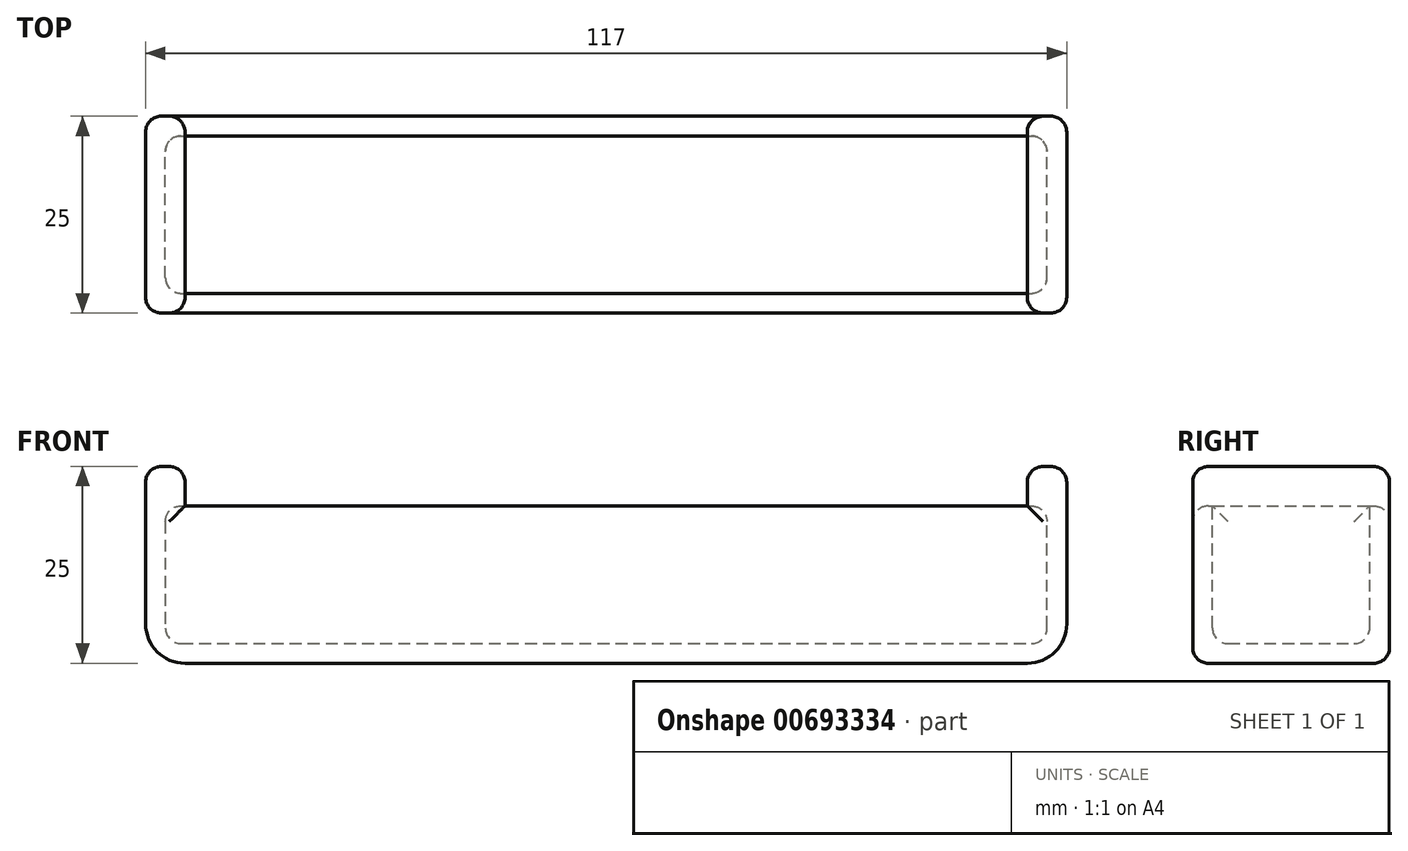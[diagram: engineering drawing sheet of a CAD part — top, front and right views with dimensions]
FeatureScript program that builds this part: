
annotation { "Feature Type Name" : "Feature", "Feature Type Description" : "" }
export const myFeature = defineFeature(function(context is Context, id is Id, definition is map)
    precondition{}
    {
        {
            var Q0;
            Q0=qCreatedBy(makeId("Front.planeOp"),FACE);
            var sketch = newSketch(context, id + "F0", { "sketchPlane" : qUnion([Q0])});
            skLineSegment(sketch, "E0", {"start": v(-39.57, 0) * mm, "end": v(67.43, 0) * mm});
            skLineSegment(sketch, "E1", {"start": v(-39.57, 0) * mm, "end": v(-39.57, 5) * mm});
            skLineSegment(sketch, "E2", {"start": v(-39.57, 5) * mm, "end": v(-44.57, 5) * mm});
            skLineSegment(sketch, "E3", {"start": v(-44.57, 5) * mm, "end": v(-44.57, -20) * mm});
            skLineSegment(sketch, "E4", {"start": v(-44.57, -20) * mm, "end": v(72.43, -20) * mm});
            skLineSegment(sketch, "E5", {"start": v(72.43, -20) * mm, "end": v(72.43, 5) * mm});
            skLineSegment(sketch, "E6", {"start": v(72.43, 5) * mm, "end": v(67.43, 5) * mm});
            skLineSegment(sketch, "E7", {"start": v(67.43, 5) * mm, "end": v(67.43, 0) * mm});
            skSolve(sketch);
        }
        {
            var Q0;
            Q0=makeQuery(id+"F0.imprint","IMPRINT",FACE,{"disambiguationData":[TD([[makeQuery(id+"F0.imprint","IMPRINT",EDGE,{"derivedFrom":sQuery(id+"F0.wireOp",EDGE,"E0")}),-1.0]])]});
            extrude(context, id + "F1", {"entities" : qUnion([Q0]), "depth" : 25 * mm, "offsetDistance" : 25 * mm});
        }
        {
            var Q0;
            Q0=makeQuery(id+"F1.opExtrude","SWEPT_FACE",FACE,{"disambiguationData":[OSD([sQuery(id+"F0.wireOp",EDGE,"E0")])]});
            shell(context, id + "F2", {"entities" : qUnion([Q0]), "thickness" : 2.5 * mm});
        }
        {
            var Q0;
            Q0=makeQuery(id+"F1.opExtrude","SWEPT_FACE",FACE,{"disambiguationData":[OSD([sQuery(id+"F0.wireOp",EDGE,"E2")])]});
            var Q1;
            Q1=makeQuery(id+"F1.opExtrude","CAP_FACE",FACE,{"disambiguationData":[OSD([sQuery(id+"F0.wireOp",EDGE,"E0"),sQuery(id+"F0.wireOp",EDGE,"E1"),sQuery(id+"F0.wireOp",EDGE,"E2"),sQuery(id+"F0.wireOp",EDGE,"E3"),sQuery(id+"F0.wireOp",EDGE,"E4"),sQuery(id+"F0.wireOp",EDGE,"E5"),sQuery(id+"F0.wireOp",EDGE,"E6"),sQuery(id+"F0.wireOp",EDGE,"E7")])],"isStart":false});
            var Q2;
            Q2=makeQuery(id+"F1.opExtrude","CAP_FACE",FACE,{"disambiguationData":[OSD([sQuery(id+"F0.wireOp",EDGE,"E0"),sQuery(id+"F0.wireOp",EDGE,"E1"),sQuery(id+"F0.wireOp",EDGE,"E2"),sQuery(id+"F0.wireOp",EDGE,"E3"),sQuery(id+"F0.wireOp",EDGE,"E4"),sQuery(id+"F0.wireOp",EDGE,"E5"),sQuery(id+"F0.wireOp",EDGE,"E6"),sQuery(id+"F0.wireOp",EDGE,"E7")])],"isStart":true});
            var Q3;
            Q3=makeQuery(id+"F2.opShell","OFFSET_FACE",FACE,{"disambiguationData":[OSD([sQuery(id+"F0.wireOp",EDGE,"E4")])]});
            var Q4;
            Q4=makeQuery(id+"F2.opShell","OFFSET_FACE",FACE,{"disambiguationData":[OSD([sQuery(id+"F0.wireOp",EDGE,"E3")])]});
            var Q5;
            Q5=makeQuery(id+"F2.opShell","OFFSET_FACE",FACE,{"disambiguationData":[OSD([sQuery(id+"F0.wireOp",EDGE,"E5")])]});
            var Q6;
            Q6=makeQuery(id+"F1.opExtrude","SWEPT_EDGE",EDGE,{"disambiguationData":[OSD([sQuery(id+"F0.wireOp",EDGE,"E5"),sQuery(id+"F0.wireOp",EDGE,"E6")])]});
            var Q7;
            Q7=makeQuery(id+"F1.opExtrude","SWEPT_FACE",FACE,{"disambiguationData":[OSD([sQuery(id+"F0.wireOp",EDGE,"E6")])]});
            fillet(context, id + "F3", {"entities" : qUnion([Q0, Q1, Q2, Q3, Q4, Q5, Q6, Q7]), "radius" : 2 * mm, "tangentPropagation" : true, "allowEdgeOverflow" : false});
        }
        {
            var Q0;
            Q0=makeQuery(id+"F1.opExtrude","SWEPT_EDGE",EDGE,{"disambiguationData":[OSD([sQuery(id+"F0.wireOp",EDGE,"E4"),sQuery(id+"F0.wireOp",EDGE,"E5")])]});
            var Q1;
            Q1=makeQuery(id+"F1.opExtrude","SWEPT_EDGE",EDGE,{"disambiguationData":[OSD([sQuery(id+"F0.wireOp",EDGE,"E3"),sQuery(id+"F0.wireOp",EDGE,"E4")])]});
            fillet(context, id + "F4", {"entities" : qUnion([Q0, Q1]), "radius" : 5 * mm, "tangentPropagation" : true, "allowEdgeOverflow" : false});
        }
    });
